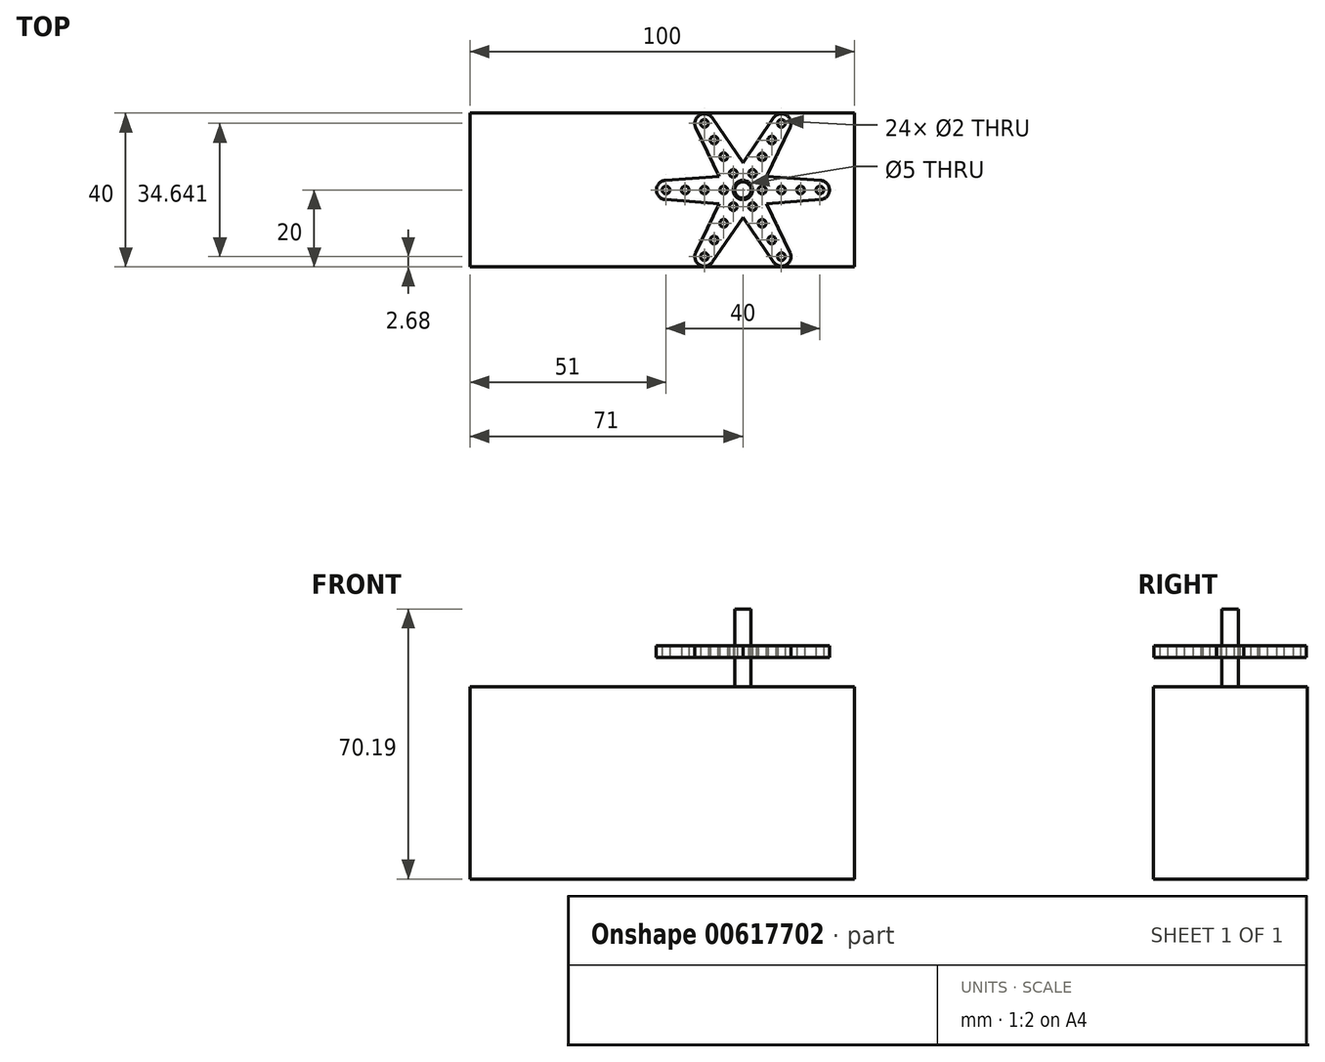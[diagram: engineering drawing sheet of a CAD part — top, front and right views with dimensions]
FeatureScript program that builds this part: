
annotation { "Feature Type Name" : "Feature", "Feature Type Description" : "" }
export const myFeature = defineFeature(function(context is Context, id is Id, definition is map)
    precondition{}
    {
        {
            var Q0;
            Q0=qCreatedBy(makeId("Top.planeOp"),FACE);
            var sketch = newSketch(context, id + "F0", { "sketchPlane" : qUnion([Q0])});
            skCircle(sketch, "E0", {"center": v(0, 0) * mm, "radius": 2.5 * mm});
            skArc(sketch, "E1", {"start": v(20.19, -2.5) * mm, "mid": v(22.5, 0) * mm, "end": v(20.19, 2.5) * mm});
            skLineSegment(sketch, "E2", {"start": v(20.19, 2.5) * mm, "end": v(6.15, 3.55) * mm});
            skLineSegment(sketch, "E3", {"start": v(6.15, -3.55) * mm, "end": v(20.19, -2.5) * mm});
            skArc(sketch, "E4.1.0", {"start": v(12.25, 16.24) * mm, "mid": v(11.25, 19.49) * mm, "end": v(7.93, 18.73) * mm});
            skLineSegment(sketch, "E4.1.1", {"start": v(7.93, 18.73) * mm, "end": v(0, 7.1) * mm});
            skLineSegment(sketch, "E4.1.2", {"start": v(6.15, 3.55) * mm, "end": v(12.25, 16.24) * mm});
            skArc(sketch, "E4.2.0", {"start": v(-7.93, 18.73) * mm, "mid": v(-11.25, 19.49) * mm, "end": v(-12.25, 16.24) * mm});
            skLineSegment(sketch, "E4.2.1", {"start": v(-12.25, 16.24) * mm, "end": v(-6.15, 3.55) * mm});
            skLineSegment(sketch, "E4.2.2", {"start": v(0, 7.1) * mm, "end": v(-7.93, 18.73) * mm});
            skArc(sketch, "E4.3.0", {"start": v(-20.19, 2.5) * mm, "mid": v(-22.5, 0) * mm, "end": v(-20.19, -2.5) * mm});
            skLineSegment(sketch, "E4.3.1", {"start": v(-20.19, -2.5) * mm, "end": v(-6.15, -3.55) * mm});
            skLineSegment(sketch, "E4.3.2", {"start": v(-6.15, 3.55) * mm, "end": v(-20.19, 2.5) * mm});
            skArc(sketch, "E4.4.0", {"start": v(-12.25, -16.24) * mm, "mid": v(-11.25, -19.49) * mm, "end": v(-7.93, -18.73) * mm});
            skLineSegment(sketch, "E4.4.1", {"start": v(-7.93, -18.73) * mm, "end": v(0, -7.1) * mm});
            skLineSegment(sketch, "E4.4.2", {"start": v(-6.15, -3.55) * mm, "end": v(-12.25, -16.24) * mm});
            skArc(sketch, "E4.5.0", {"start": v(7.93, -18.73) * mm, "mid": v(11.25, -19.49) * mm, "end": v(12.25, -16.24) * mm});
            skLineSegment(sketch, "E4.5.1", {"start": v(12.25, -16.24) * mm, "end": v(6.15, -3.55) * mm});
            skLineSegment(sketch, "E4.5.2", {"start": v(0, -7.1) * mm, "end": v(7.93, -18.73) * mm});
            skCircle(sketch, "E5", {"center": v(5, 0) * mm, "radius": 1 * mm});
            skCircle(sketch, "E6.1.0.0", {"center": v(10, 0) * mm, "radius": 1 * mm});
            skCircle(sketch, "E6.2.0.0", {"center": v(15, 0) * mm, "radius": 1 * mm});
            skCircle(sketch, "E6.3.0.0", {"center": v(20, 0) * mm, "radius": 1 * mm});
            skLineSegment(sketch, "E6.direction1", {"start": v(5, 0) * mm, "end": v(10, 0) * mm, "construction": true});
            skCircle(sketch, "E7.1.0", {"center": v(2.5, 4.33) * mm, "radius": 1 * mm});
            skCircle(sketch, "E7.1.1", {"center": v(7.5, 13) * mm, "radius": 1 * mm});
            skCircle(sketch, "E7.1.2", {"center": v(5, 8.66) * mm, "radius": 1 * mm});
            skLineSegment(sketch, "E7.1.3", {"start": v(2.5, 4.33) * mm, "end": v(5, 8.66) * mm, "construction": true});
            skCircle(sketch, "E7.1.4", {"center": v(10, 17.32) * mm, "radius": 1 * mm});
            skCircle(sketch, "E7.2.0", {"center": v(-2.5, 4.33) * mm, "radius": 1 * mm});
            skCircle(sketch, "E7.2.1", {"center": v(-7.5, 13) * mm, "radius": 1 * mm});
            skCircle(sketch, "E7.2.2", {"center": v(-5, 8.66) * mm, "radius": 1 * mm});
            skLineSegment(sketch, "E7.2.3", {"start": v(-2.5, 4.33) * mm, "end": v(-5, 8.66) * mm, "construction": true});
            skCircle(sketch, "E7.2.4", {"center": v(-10, 17.32) * mm, "radius": 1 * mm});
            skCircle(sketch, "E7.3.0", {"center": v(-5, 0) * mm, "radius": 1 * mm});
            skCircle(sketch, "E7.3.1", {"center": v(-15, 0) * mm, "radius": 1 * mm});
            skCircle(sketch, "E7.3.2", {"center": v(-10, 0) * mm, "radius": 1 * mm});
            skLineSegment(sketch, "E7.3.3", {"start": v(-5, 0) * mm, "end": v(-10, 0) * mm, "construction": true});
            skCircle(sketch, "E7.3.4", {"center": v(-20, 0) * mm, "radius": 1 * mm});
            skCircle(sketch, "E7.4.0", {"center": v(-2.5, -4.33) * mm, "radius": 1 * mm});
            skCircle(sketch, "E7.4.1", {"center": v(-7.5, -13) * mm, "radius": 1 * mm});
            skCircle(sketch, "E7.4.2", {"center": v(-5, -8.66) * mm, "radius": 1 * mm});
            skLineSegment(sketch, "E7.4.3", {"start": v(-2.5, -4.33) * mm, "end": v(-5, -8.66) * mm, "construction": true});
            skCircle(sketch, "E7.4.4", {"center": v(-10, -17.32) * mm, "radius": 1 * mm});
            skCircle(sketch, "E7.5.0", {"center": v(2.5, -4.33) * mm, "radius": 1 * mm});
            skCircle(sketch, "E7.5.1", {"center": v(7.5, -13) * mm, "radius": 1 * mm});
            skCircle(sketch, "E7.5.2", {"center": v(5, -8.66) * mm, "radius": 1 * mm});
            skLineSegment(sketch, "E7.5.3", {"start": v(2.5, -4.33) * mm, "end": v(5, -8.66) * mm, "construction": true});
            skCircle(sketch, "E7.5.4", {"center": v(10, -17.32) * mm, "radius": 1 * mm});
            skSolve(sketch);
        }
        {
            var Q0;
            Q0 = qSketchRegion(id + "F0", true);
            extrude(context, id + "F1", {"entities" : qUnion([Q0]), "depth" : 3 * mm, "offsetDistance" : 25 * mm});
        }
        {
            var Q0;
            Q0=qCreatedBy(makeId("Top.planeOp"),FACE);
            var sketch = newSketch(context, id + "F2", { "sketchPlane" : qUnion([Q0])});
            skCircle(sketch, "E8", {"center": v(0, 0) * mm, "radius": 2.12 * mm});
            skSolve(sketch);
        }
        {
            var Q0;
            Q0 = qSketchRegion(id + "F2", true);
            extrude(context, id + "F3", {"entities" : qUnion([Q0]), "endBound" : BoundingType.SYMMETRIC, "oppositeDirection" : true, "depth" : 25 * mm, "offsetDistance" : 25 * mm});
        }
        {
            var Q0;
            Q0=qCreatedBy(makeId("Front.planeOp"),FACE);
            var sketch = newSketch(context, id + "F4", { "sketchPlane" : qUnion([Q0])});
            skLineSegment(sketch, "E9.bottom", {"start": v(29, -7.7) * mm, "end": v(-71, -7.7) * mm});
            skLineSegment(sketch, "E9.top", {"start": v(29, -57.7) * mm, "end": v(-71, -57.7) * mm});
            skLineSegment(sketch, "E9.left", {"start": v(29, -7.7) * mm, "end": v(29, -57.7) * mm});
            skLineSegment(sketch, "E9.right", {"start": v(-71, -7.7) * mm, "end": v(-71, -57.7) * mm});
            skSolve(sketch);
        }
        {
            var Q0;
            Q0 = qSketchRegion(id + "F4", true);
            extrude(context, id + "F5", {"entities" : qUnion([Q0]), "operationType" : NewBodyOperationType.ADD, "endBound" : BoundingType.SYMMETRIC, "depth" : 40 * mm, "offsetDistance" : 25 * mm});
        }
    });
